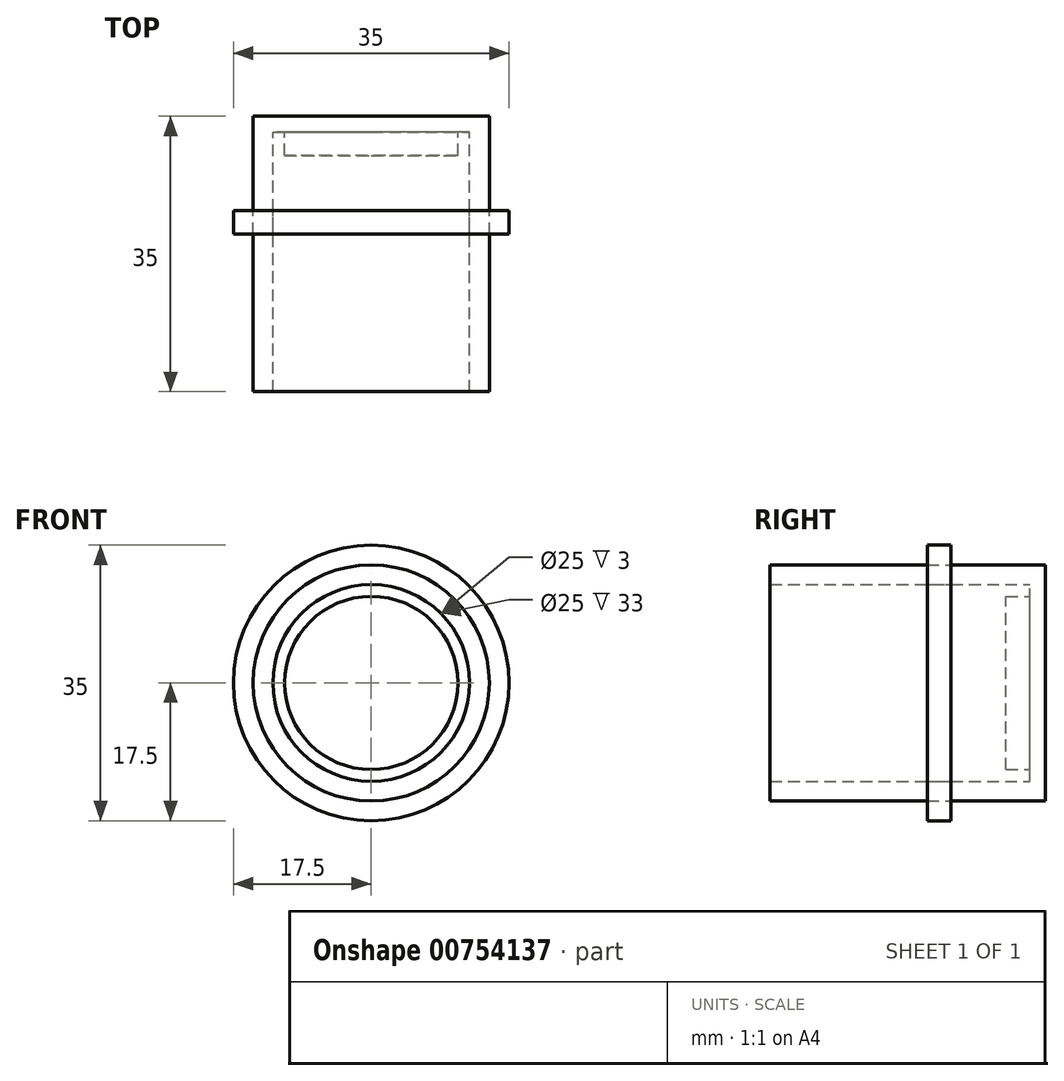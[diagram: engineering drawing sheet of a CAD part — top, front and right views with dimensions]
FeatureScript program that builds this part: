
annotation { "Feature Type Name" : "Feature", "Feature Type Description" : "" }
export const myFeature = defineFeature(function(context is Context, id is Id, definition is map)
    precondition{}
    {
        {
            var Q0;
            Q0=qCreatedBy(makeId("Front.planeOp"),FACE);
            var sketch = newSketch(context, id + "F0", { "sketchPlane" : qUnion([Q0])});
            skCircle(sketch, "E0", {"center": v(0, 0) * mm, "radius": 15 * mm});
            skCircle(sketch, "E1", {"center": v(0, 0) * mm, "radius": 17.5 * mm});
            skLineSegment(sketch, "E2.bottom", {"start": v(22.5, -22.5) * mm, "end": v(-22.5, -22.5) * mm});
            skLineSegment(sketch, "E2.top", {"start": v(22.5, 22.5) * mm, "end": v(-22.5, 22.5) * mm});
            skLineSegment(sketch, "E2.left", {"start": v(22.5, -22.5) * mm, "end": v(22.5, 22.5) * mm});
            skLineSegment(sketch, "E2.right", {"start": v(-22.5, -22.5) * mm, "end": v(-22.5, 22.5) * mm});
            skCircle(sketch, "E3", {"center": v(0, 0) * mm, "radius": 12.5 * mm});
            skCircle(sketch, "E4", {"center": v(0, 0) * mm, "radius": 11 * mm});
            skSolve(sketch);
        }
        {
            var Q0;
            Q0=makeQuery(id+"F0.imprint","IMPRINT",FACE,{"disambiguationData":[TD([[makeQuery(id+"F0.imprint","IMPRINT",EDGE,{"derivedFrom":sQuery(id+"F0.wireOp",EDGE,"E0")}),1.0]])]});
            extrude(context, id + "F1", {"entities" : qUnion([Q0]), "depth" : 35 * mm, "offsetDistance" : 25 * mm});
        }
        {
            var Q0;
            Q0=makeQuery(id+"F0.imprint","IMPRINT",FACE,{"disambiguationData":[TD([[makeQuery(id+"F0.imprint","IMPRINT",EDGE,{"derivedFrom":sQuery(id+"F0.wireOp",EDGE,"E3")}),1.0]])]});
            var Q1;
            Q1=sQuery(id+"F0.wireOp",EDGE,"E3");
            extrude(context, id + "F2", {"entities" : qUnion([Q0]), "operationType" : NewBodyOperationType.ADD, "surfaceOperationType" : NewSurfaceOperationType.ADD, "surfaceEntities" : qUnion([Q1]), "depth" : 2 * mm, "offsetDistance" : 25 * mm});
        }
        {
            var Q0;
            Q0=makeQuery(id+"F0.imprint","IMPRINT",FACE,{"disambiguationData":[TD([[makeQuery(id+"F0.imprint","IMPRINT",EDGE,{"derivedFrom":sQuery(id+"F0.wireOp",EDGE,"E4")}),1.0]])]});
            extrude(context, id + "F3", {"entities" : qUnion([Q0]), "operationType" : NewBodyOperationType.ADD, "depth" : 5 * mm, "offsetDistance" : 25 * mm});
        }
        {
            var Q0;
            Q0=makeQuery(id+"F0.imprint","IMPRINT",FACE,{"disambiguationData":[TD([[makeQuery(id+"F0.imprint","IMPRINT",EDGE,{"derivedFrom":sQuery(id+"F0.wireOp",EDGE,"E0")}),-1.0]])]});
            var Q1;
            Q1=makeQuery(id+"F0.imprint","IMPRINT",FACE,{"disambiguationData":[TD([[makeQuery(id+"F0.imprint","IMPRINT",EDGE,{"derivedFrom":sQuery(id+"F0.wireOp",EDGE,"E0")}),1.0]])]});
            extrude(context, id + "F4", {"entities" : qUnion([Q0, Q1]), "depth" : 3 * mm, "offsetDistance" : 25 * mm});
        }
        {
            var Q0;
            Q0=makeQuery(id+"F4.opExtrude","SWEPT_BODY",BODY,{"disambiguationData":[OSD([sQuery(id+"F0.wireOp",EDGE,"E0"),sQuery(id+"F0.wireOp",EDGE,"E1")])]});
            var Q1;
            Q1=makeQuery(id+"F1.opExtrude","CAP_EDGE",EDGE,{"disambiguationData":[OSD([sQuery(id+"F0.wireOp",EDGE,"E0")])],"isStart":false});
            var Q2;
            Q2=makeQuery(id+"F1.opExtrude","SWEPT_FACE",FACE,{"disambiguationData":[OSD([sQuery(id+"F0.wireOp",EDGE,"E0")])]});
            transform(context, id + "F5", {"entities" : qUnion([Q0]), "transformType" : TransformType.TRANSLATION_DISTANCE, "transformDirection" : qUnion([Q2]), "distance" : 12 * mm, "oppositeDirection" : true, "makeCopy" : false});
        }
    });
